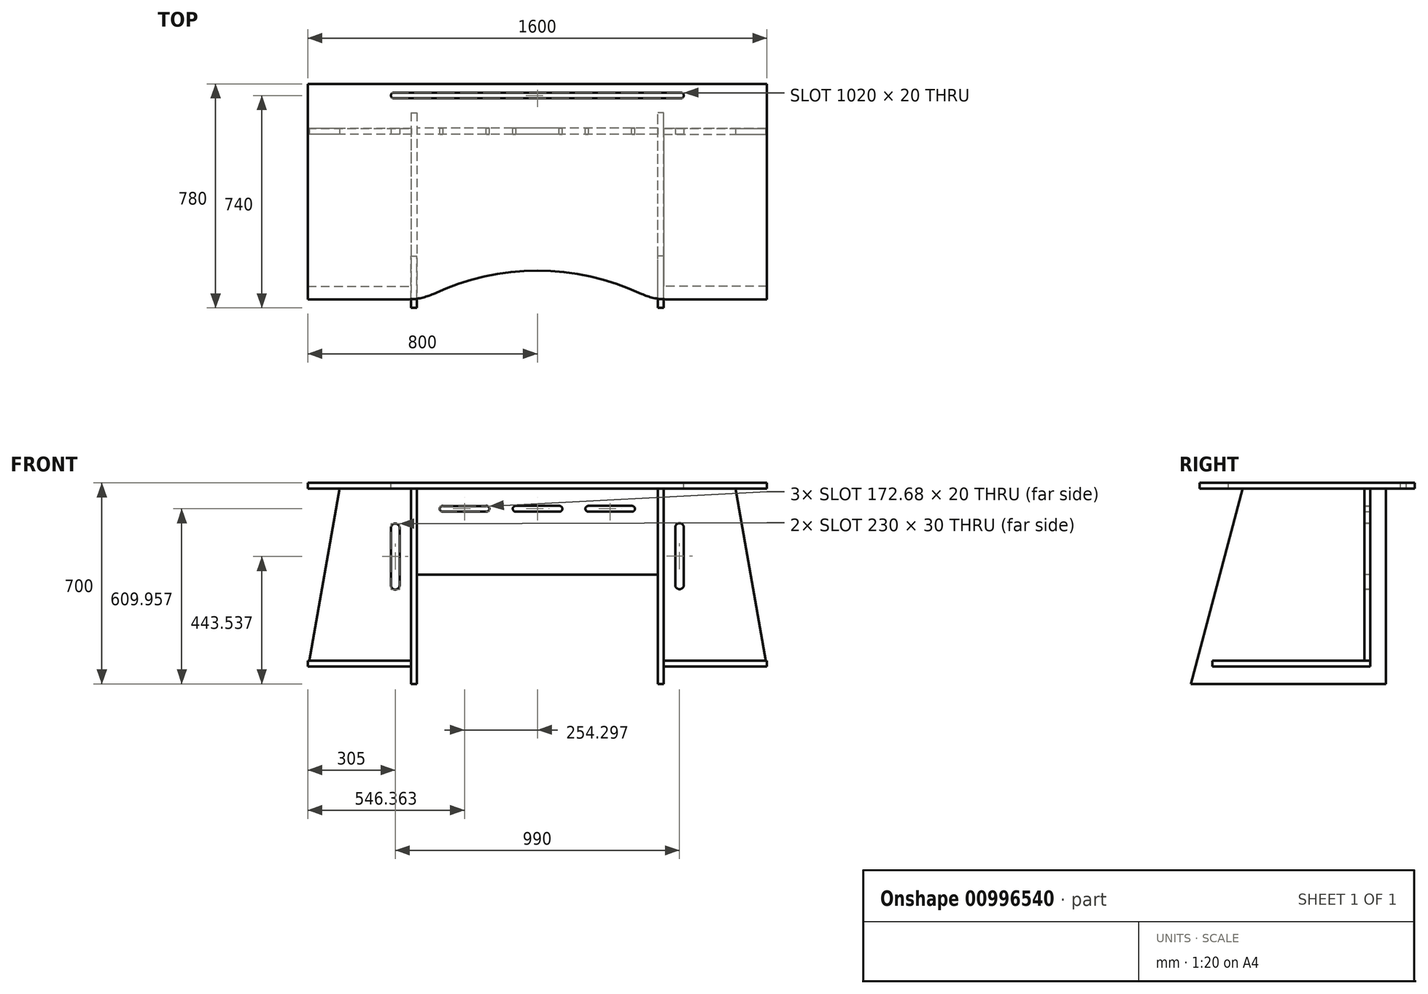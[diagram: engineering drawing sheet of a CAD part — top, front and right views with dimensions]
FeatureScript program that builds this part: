
annotation { "Feature Type Name" : "Feature", "Feature Type Description" : "" }
export const myFeature = defineFeature(function(context is Context, id is Id, definition is map)
    precondition{}
    {
        {
            var Q0;
            Q0=qCreatedBy(makeId("Top.planeOp"),FACE);
            var sketch = newSketch(context, id + "F0", { "sketchPlane" : qUnion([Q0])});
            skLineSegment(sketch, "E0.bottom", {"start": v(800, -375) * mm, "end": v(447.21, -375) * mm});
            skLineSegment(sketch, "E0.top", {"start": v(800, 375) * mm, "end": v(-800, 375) * mm});
            skLineSegment(sketch, "E0.left", {"start": v(800, -375) * mm, "end": v(800, 375) * mm});
            skLineSegment(sketch, "E0.right", {"start": v(-800, -375) * mm, "end": v(-800, 375) * mm});
            skPoint(sketch, "E0.middle", {"position": v(0, 0) * mm});
            skLineSegment(sketch, "E1", {"start": v(0, 375) * mm, "end": v(0, -375) * mm, "construction": true});
            skArc(sketch, "E2", {"start": v(362.03, -355.95) * mm, "mid": v(0, -275) * mm, "end": v(-362.03, -355.95) * mm});
            skPoint(sketch, "E3.newPointA", {"position": v(400, -375) * mm});
            skPoint(sketch, "E3.newPointB", {"position": v(-800, -375) * mm});
            skArc(sketch, "E3.filletArc", {"start": v(362.03, -355.95) * mm, "mid": v(403.57, -370.18) * mm, "end": v(447.21, -375) * mm});
            skLineSegment(sketch, "E4", {"start": v(-800, -375) * mm, "end": v(-447.21, -375) * mm});
            skPoint(sketch, "E5.visualSharp", {"position": v(-400, -375) * mm});
            skArc(sketch, "E5.filletArc", {"start": v(-447.21, -375) * mm, "mid": v(-403.57, -370.18) * mm, "end": v(-362.03, -355.95) * mm});
            skSolve(sketch);
        }
        {
            var Q0;
            Q0=makeQuery(id+"F0.imprint","IMPRINT",FACE,{"disambiguationData":[TD([[makeQuery(id+"F0.imprint","IMPRINT",EDGE,{"derivedFrom":sQuery(id+"F0.wireOp",EDGE,"E0.bottom")}),-1.0]])]});
            extrude(context, id + "F1", {"entities" : qUnion([Q0]), "depth" : 20 * mm, "offsetDistance" : 25 * mm});
        }
        {
            var Q0;
            Q0=qCreatedBy(makeId("Right.planeOp"),FACE);
            var sketch = newSketch(context, id + "F2", { "sketchPlane" : qUnion([Q0])});
            skLineSegment(sketch, "E6.bottom", {"start": v(275, 0) * mm, "end": v(-225, 0) * mm});
            skLineSegment(sketch, "E6.top", {"start": v(275, -680) * mm, "end": v(-405, -680) * mm});
            skLineSegment(sketch, "E6.left", {"start": v(275, 0) * mm, "end": v(275, -680) * mm});
            skLineSegment(sketch, "E7", {"start": v(-405, -680) * mm, "end": v(-225, 0) * mm});
            skSolve(sketch);
        }
        {
            var Q0;
            Q0=makeQuery(id+"F2.imprint","IMPRINT",FACE,{"disambiguationData":[TD([[makeQuery(id+"F2.imprint","IMPRINT",EDGE,{"derivedFrom":sQuery(id+"F2.wireOp",EDGE,"E6.bottom")}),1.0]])]});
            extrude(context, id + "F3", {"entities" : qUnion([Q0]), "oppositeDirection" : true, "depth" : 440 * mm, "offsetDistance" : 25 * mm, "hasSecondDirection" : true, "secondDirectionOppositeDirection" : true, "secondDirectionDepth" : 420 * mm});
        }
        {
            var Q0;
            Q0=qCreatedBy(makeId("Right.planeOp"),FACE);
            var sketch = newSketch(context, id + "F4", { "sketchPlane" : qUnion([Q0])});
            skLineSegment(sketch, "E8.bottom", {"start": v(-225, 0) * mm, "end": v(275, 0) * mm});
            skLineSegment(sketch, "E8.top", {"start": v(-405, -680) * mm, "end": v(275, -680) * mm});
            skLineSegment(sketch, "E8.right", {"start": v(275, 0) * mm, "end": v(275, -680) * mm});
            skLineSegment(sketch, "E9", {"start": v(-405, -680) * mm, "end": v(-225, 0) * mm});
            skPoint(sketch, "E10.orphan", {"position": v(-405, 0) * mm});
            skSolve(sketch);
        }
        {
            var Q0;
            Q0=makeQuery(id+"F4.imprint","IMPRINT",FACE,{"disambiguationData":[TD([[makeQuery(id+"F4.imprint","IMPRINT",EDGE,{"derivedFrom":sQuery(id+"F4.wireOp",EDGE,"E8.bottom")}),-1.0]])]});
            extrude(context, id + "F5", {"entities" : qUnion([Q0]), "operationType" : NewBodyOperationType.ADD, "depth" : 440 * mm, "offsetDistance" : 25 * mm, "hasSecondDirection" : true, "secondDirectionOppositeDirection" : false, "secondDirectionDepth" : 420 * mm});
        }
        {
            var Q0;
            Q0=qCreatedBy(makeId("Front.planeOp"),FACE);
            var sketch = newSketch(context, id + "F6", { "sketchPlane" : qUnion([Q0])});
            skLineSegment(sketch, "E11.bottom", {"start": v(420, 0) * mm, "end": v(-420, 0) * mm});
            skLineSegment(sketch, "E11.top", {"start": v(420, -300) * mm, "end": v(-420, -300) * mm});
            skLineSegment(sketch, "E11.left", {"start": v(420, 0) * mm, "end": v(420, -300) * mm});
            skLineSegment(sketch, "E11.right", {"start": v(-420, 0) * mm, "end": v(-420, -300) * mm});
            skSolve(sketch);
        }
        {
            var Q0;
            Q0=makeQuery(id+"F6.imprint","IMPRINT",FACE,{"disambiguationData":[TD([[makeQuery(id+"F6.imprint","IMPRINT",EDGE,{"derivedFrom":sQuery(id+"F6.wireOp",EDGE,"E11.bottom")}),1.0]])]});
            extrude(context, id + "F7", {"entities" : qUnion([Q0]), "oppositeDirection" : true, "depth" : 221 * mm, "offsetDistance" : 25 * mm, "hasSecondDirection" : true, "secondDirectionOppositeDirection" : true, "secondDirectionDepth" : 200 * mm});
        }
        {
            var Q0;
            Q0=qCreatedBy(makeId("Front.planeOp"),FACE);
            var sketch = newSketch(context, id + "F8", { "sketchPlane" : qUnion([Q0])});
            skLineSegment(sketch, "E12.bottom", {"start": v(-438.73, 0) * mm, "end": v(-688.73, 0) * mm});
            skLineSegment(sketch, "E12.top", {"start": v(-438.73, -599.48) * mm, "end": v(-794.6, -599.48) * mm});
            skLineSegment(sketch, "E12.left", {"start": v(-438.73, 0) * mm, "end": v(-438.73, -599.48) * mm});
            skLineSegment(sketch, "E13", {"start": v(-794.6, -599.48) * mm, "end": v(-794.6, -740.66) * mm, "construction": true});
            skLineSegment(sketch, "E14", {"start": v(-688.73, 0) * mm, "end": v(-794.6, -599.48) * mm});
            skPoint(sketch, "E12.right.start.orphan", {"position": v(-794.6, 0) * mm});
            skSolve(sketch);
        }
        {
            var Q0;
            Q0=makeQuery(id+"F8.imprint","IMPRINT",FACE,{"disambiguationData":[TD([[makeQuery(id+"F8.imprint","IMPRINT",EDGE,{"derivedFrom":sQuery(id+"F8.wireOp",EDGE,"E12.bottom")}),1.0]])]});
            extrude(context, id + "F9", {"entities" : qUnion([Q0]), "oppositeDirection" : true, "depth" : 220 * mm, "offsetDistance" : 25 * mm, "hasSecondDirection" : true, "secondDirectionOppositeDirection" : true, "secondDirectionDepth" : 200 * mm});
        }
        {
            var Q0;
            Q0=qCreatedBy(makeId("Right.planeOp"),FACE);
            var sketch = newSketch(context, id + "F10", { "sketchPlane" : qUnion([Q0])});
            skLineSegment(sketch, "E15.bottom", {"start": v(220.27, -599.5) * mm, "end": v(-329.73, -599.5) * mm});
            skLineSegment(sketch, "E15.top", {"start": v(220.27, -619.5) * mm, "end": v(-329.73, -619.5) * mm});
            skLineSegment(sketch, "E15.left", {"start": v(220.27, -599.5) * mm, "end": v(220.27, -619.5) * mm});
            skLineSegment(sketch, "E15.right", {"start": v(-329.73, -599.5) * mm, "end": v(-329.73, -619.5) * mm});
            skSolve(sketch);
        }
        {
            var Q0;
            Q0=makeQuery(id+"F10.imprint","IMPRINT",FACE,{"disambiguationData":[TD([[makeQuery(id+"F10.imprint","IMPRINT",EDGE,{"derivedFrom":sQuery(id+"F10.wireOp",EDGE,"E15.bottom")}),1.0]])]});
            extrude(context, id + "F11", {"entities" : qUnion([Q0]), "operationType" : NewBodyOperationType.ADD, "oppositeDirection" : true, "depth" : 800 * mm, "offsetDistance" : 25 * mm, "hasSecondDirection" : true, "secondDirectionOppositeDirection" : true, "secondDirectionDepth" : 440 * mm});
        }
        {
            var Q0;
            Q0=makeQuery(id+"F9.opExtrude","CAP_FACE",FACE,{"disambiguationData":[OSD([sQuery(id+"F8.wireOp",EDGE,"E12.bottom"),sQuery(id+"F8.wireOp",EDGE,"E12.top"),sQuery(id+"F8.wireOp",EDGE,"E12.left"),sQuery(id+"F8.wireOp",EDGE,"E14")])],"isStart":true});
            var sketch = newSketch(context, id + "F12", { "sketchPlane" : qUnion([Q0])});
            skLineSegment(sketch, "E16", {"start": v(-497.35, -207.21) * mm, "end": v(-497.35, -384.66) * mm, "construction": true});
            skLineSegment(sketch, "E17", {"start": v(-510, -136.46) * mm, "end": v(-510, -336.46) * mm});
            skLineSegment(sketch, "E18", {"start": v(-480, -136.46) * mm, "end": v(-480, -336.46) * mm});
            skArc(sketch, "E19", {"start": v(-480, -136.46) * mm, "mid": v(-495, -121.46) * mm, "end": v(-510, -136.46) * mm});
            skArc(sketch, "E20", {"start": v(-510, -336.46) * mm, "mid": v(-495, -351.46) * mm, "end": v(-480, -336.46) * mm});
            skSolve(sketch);
        }
        {
            var Q0;
            Q0=makeQuery(id+"F12.imprint","IMPRINT",FACE,{"disambiguationData":[TD([[makeQuery(id+"F12.imprint","IMPRINT",EDGE,{"derivedFrom":sQuery(id+"F12.wireOp",EDGE,"E17")}),1.0]])]});
            extrude(context, id + "F13", {"entities" : qUnion([Q0]), "operationType" : NewBodyOperationType.REMOVE, "oppositeDirection" : true, "depth" : 61 * mm, "offsetDistance" : 25 * mm});
        }
        {
            var Q0;
            Q0=makeQuery(id+"F1.opExtrude","CAP_FACE",FACE,{"disambiguationData":[OSD([sQuery(id+"F0.wireOp",EDGE,"E0.bottom"),sQuery(id+"F0.wireOp",EDGE,"E0.top"),sQuery(id+"F0.wireOp",EDGE,"E0.left"),sQuery(id+"F0.wireOp",EDGE,"E0.right"),sQuery(id+"F0.wireOp",EDGE,"E2"),sQuery(id+"F0.wireOp",EDGE,"E3.filletArc"),sQuery(id+"F0.wireOp",EDGE,"E4"),sQuery(id+"F0.wireOp",EDGE,"E5.filletArc")])],"isStart":false});
            var sketch = newSketch(context, id + "F14", { "sketchPlane" : qUnion([Q0])});
            skLineSegment(sketch, "E21", {"start": v(0, 375) * mm, "end": v(0, -425.98) * mm, "construction": true});
            skLineSegment(sketch, "E22.bottom", {"start": v(-500, 345) * mm, "end": v(500, 345) * mm});
            skLineSegment(sketch, "E22.top", {"start": v(-500, 325) * mm, "end": v(500, 325) * mm});
            skArc(sketch, "E23", {"start": v(-500, 345) * mm, "mid": v(-510, 335) * mm, "end": v(-500, 325) * mm});
            skArc(sketch, "E24", {"start": v(500, 325) * mm, "mid": v(510, 335) * mm, "end": v(500, 345) * mm});
            skSolve(sketch);
        }
        {
            var Q0;
            Q0=makeQuery(id+"F14.imprint","IMPRINT",FACE,{"disambiguationData":[TD([[makeQuery(id+"F14.imprint","IMPRINT",EDGE,{"derivedFrom":sQuery(id+"F14.wireOp",EDGE,"E22.bottom")}),-1.0]])]});
            extrude(context, id + "F15", {"entities" : qUnion([Q0]), "operationType" : NewBodyOperationType.REMOVE, "flatOperationType" : FlatOperationType.REMOVE, "endBound" : BoundingType.UP_TO_NEXT, "oppositeDirection" : true, "depth" : 64 * mm, "offsetDistance" : 25 * mm, "domain" : OperationDomain.MODEL});
        }
        {
            var Q0;
            Q0=makeQuery(id+"F9.opExtrude","CAP_FACE",FACE,{"disambiguationData":[OSD([sQuery(id+"F8.wireOp",EDGE,"E12.bottom"),sQuery(id+"F8.wireOp",EDGE,"E12.top"),sQuery(id+"F8.wireOp",EDGE,"E12.left"),sQuery(id+"F8.wireOp",EDGE,"E14")])],"isStart":true});
            var sketch = newSketch(context, id + "F16", { "sketchPlane" : qUnion([Q0])});
            skLineSegment(sketch, "E25.bottom", {"start": v(440, 0) * mm, "end": v(690, 0) * mm});
            skLineSegment(sketch, "E25.top", {"start": v(440, -599.48) * mm, "end": v(795.88, -599.48) * mm});
            skLineSegment(sketch, "E25.left", {"start": v(440, 0) * mm, "end": v(440, -599.48) * mm});
            skLineSegment(sketch, "E26", {"start": v(795.88, 14.47) * mm, "end": v(795.88, 0) * mm, "construction": true});
            skLineSegment(sketch, "E27", {"start": v(690, 0) * mm, "end": v(795.88, -599.48) * mm});
            skLineSegment(sketch, "E28.trimOffspring", {"start": v(795.88, -599.48) * mm, "end": v(795.88, -713.84) * mm, "construction": true});
            skSolve(sketch);
        }
        {
            var Q0;
            Q0=makeQuery(id+"F16.imprint","IMPRINT",FACE,{"disambiguationData":[TD([[makeQuery(id+"F16.imprint","IMPRINT",EDGE,{"derivedFrom":sQuery(id+"F16.wireOp",EDGE,"E25.bottom")}),-1.0]])]});
            extrude(context, id + "F17", {"entities" : qUnion([Q0]), "operationType" : NewBodyOperationType.ADD, "oppositeDirection" : true, "depth" : 20 * mm, "offsetDistance" : 25 * mm});
        }
        {
            var Q0;
            Q0=qCreatedBy(makeId("Right.planeOp"),FACE);
            var sketch = newSketch(context, id + "F18", { "sketchPlane" : qUnion([Q0])});
            skLineSegment(sketch, "E29.bottom", {"start": v(219.62, -599.48) * mm, "end": v(-330.38, -599.48) * mm});
            skLineSegment(sketch, "E29.top", {"start": v(219.62, -619.48) * mm, "end": v(-330.38, -619.48) * mm});
            skLineSegment(sketch, "E29.left", {"start": v(219.62, -599.48) * mm, "end": v(219.62, -619.48) * mm});
            skLineSegment(sketch, "E29.right", {"start": v(-330.38, -599.48) * mm, "end": v(-330.38, -619.48) * mm});
            skSolve(sketch);
        }
        {
            var Q0;
            Q0 = qSketchRegion(id + "F18", true);
            extrude(context, id + "F19", {"entities" : qUnion([Q0]), "operationType" : NewBodyOperationType.ADD, "depth" : 800 * mm, "offsetDistance" : 25 * mm, "hasSecondDirection" : true, "secondDirectionOppositeDirection" : false, "secondDirectionDepth" : 440 * mm});
        }
        {
            var Q0;
            Q0=makeQuery(id+"F17.opExtrude","CAP_FACE",FACE,{"disambiguationData":[OSD([sQuery(id+"F16.wireOp",EDGE,"E25.bottom"),sQuery(id+"F16.wireOp",EDGE,"E25.top"),sQuery(id+"F16.wireOp",EDGE,"E25.left"),sQuery(id+"F16.wireOp",EDGE,"E27")])],"isStart":true});
            var sketch = newSketch(context, id + "F20", { "sketchPlane" : qUnion([Q0])});
            skLineSegment(sketch, "E30.left", {"start": v(480, -135.02) * mm, "end": v(480, -335.02) * mm});
            skLineSegment(sketch, "E30.right", {"start": v(510, -135.02) * mm, "end": v(510, -335.02) * mm});
            skArc(sketch, "E31", {"start": v(510, -135.02) * mm, "mid": v(495, -120.02) * mm, "end": v(480, -135.02) * mm});
            skArc(sketch, "E32", {"start": v(480, -335.02) * mm, "mid": v(495, -350.02) * mm, "end": v(510, -335.02) * mm});
            skLineSegment(sketch, "E33", {"start": v(-496.31, -119.88) * mm, "end": v(594.19, -119.88) * mm, "construction": true});
            skSolve(sketch);
        }
        {
            var Q0;
            Q0=makeQuery(id+"F20.imprint","IMPRINT",FACE,{"disambiguationData":[TD([[makeQuery(id+"F20.imprint","IMPRINT",EDGE,{"derivedFrom":sQuery(id+"F20.wireOp",EDGE,"E30.left")}),1.0]])]});
            extrude(context, id + "F21", {"entities" : qUnion([Q0]), "operationType" : NewBodyOperationType.REMOVE, "endBound" : BoundingType.UP_TO_NEXT, "oppositeDirection" : true, "depth" : 47 * mm, "offsetDistance" : 25 * mm});
        }
        {
            var Q0;
            Q0=makeQuery(id+"F7.opExtrude","CAP_FACE",FACE,{"disambiguationData":[OSD([sQuery(id+"F6.wireOp",EDGE,"E11.bottom"),sQuery(id+"F6.wireOp",EDGE,"E11.top"),sQuery(id+"F6.wireOp",EDGE,"E11.left"),sQuery(id+"F6.wireOp",EDGE,"E11.right")])],"isStart":false});
            var sketch = newSketch(context, id + "F22", { "sketchPlane" : qUnion([Q0])});
            skLineSegment(sketch, "E34.bottom", {"start": v(-328.64, -60) * mm, "end": v(-178.64, -60) * mm});
            skLineSegment(sketch, "E34.top", {"start": v(-329.96, -80) * mm, "end": v(-177.32, -80) * mm});
            skArc(sketch, "E35", {"start": v(-328.64, -60) * mm, "mid": v(-339.98, -69.3) * mm, "end": v(-329.96, -80) * mm});
            skArc(sketch, "E36", {"start": v(-177.32, -80) * mm, "mid": v(-167.3, -69.3) * mm, "end": v(-178.64, -60) * mm});
            skLineSegment(sketch, "E37.bottom", {"start": v(178.64, -60.04) * mm, "end": v(328.64, -60.04) * mm});
            skLineSegment(sketch, "E37.top", {"start": v(177.32, -80.04) * mm, "end": v(329.96, -80.04) * mm});
            skArc(sketch, "E38", {"start": v(178.64, -60.04) * mm, "mid": v(167.3, -69.34) * mm, "end": v(177.32, -80.04) * mm});
            skArc(sketch, "E39", {"start": v(329.96, -80.04) * mm, "mid": v(339.98, -69.34) * mm, "end": v(328.64, -60.04) * mm});
            skLineSegment(sketch, "E40.bottom", {"start": v(-75.66, -60) * mm, "end": v(74.34, -60) * mm});
            skLineSegment(sketch, "E40.top", {"start": v(-76.98, -80) * mm, "end": v(75.66, -80) * mm});
            skArc(sketch, "E41", {"start": v(-75.66, -60) * mm, "mid": v(-87, -69.3) * mm, "end": v(-76.98, -80) * mm});
            skArc(sketch, "E42", {"start": v(75.66, -80) * mm, "mid": v(85.68, -69.3) * mm, "end": v(74.34, -60) * mm});
            skLineSegment(sketch, "E43", {"start": v(0, 0) * mm, "end": v(0, -233.21) * mm, "construction": true});
            skLineSegment(sketch, "E44", {"start": v(74.34, -60) * mm, "end": v(-76.98, -80) * mm, "construction": true});
            skLineSegment(sketch, "E45", {"start": v(-75.66, -60) * mm, "end": v(75.66, -80) * mm});
            skPoint(sketch, "E46", {"position": v(0, -70) * mm});
            skLineSegment(sketch, "E47", {"start": v(420, -70) * mm, "end": v(-420, -70) * mm, "construction": true});
            skSolve(sketch);
        }
        {
            var Q0;
            Q0=makeQuery(id+"F22.imprint","IMPRINT",FACE,{"disambiguationData":[TD([[makeQuery(id+"F22.imprint","IMPRINT",EDGE,{"derivedFrom":sQuery(id+"F22.wireOp",EDGE,"E34.bottom")}),-1.0]])]});
            extrude(context, id + "F23", {"entities" : qUnion([Q0]), "operationType" : NewBodyOperationType.REMOVE, "endBound" : BoundingType.UP_TO_NEXT, "oppositeDirection" : true, "depth" : 25 * mm, "offsetDistance" : 25 * mm});
        }
        {
            var Q0;
            Q0=makeQuery(id+"F22.imprint","IMPRINT",FACE,{"disambiguationData":[TD([[makeQuery(id+"F22.imprint","IMPRINT",EDGE,{"derivedFrom":sQuery(id+"F22.wireOp",EDGE,"E40.top")}),1.0]])]});
            var Q1;
            Q1=makeQuery(id+"F22.imprint","IMPRINT",FACE,{"disambiguationData":[TD([[makeQuery(id+"F22.imprint","IMPRINT",EDGE,{"derivedFrom":sQuery(id+"F22.wireOp",EDGE,"E40.bottom")}),-1.0]])]});
            var Q2;
            Q2=makeQuery(id+"F22.imprint","IMPRINT",FACE,{"disambiguationData":[TD([[makeQuery(id+"F22.imprint","IMPRINT",EDGE,{"derivedFrom":sQuery(id+"F22.wireOp",EDGE,"E37.bottom")}),-1.0]])]});
            extrude(context, id + "F24", {"entities" : qUnion([Q0, Q1, Q2]), "operationType" : NewBodyOperationType.REMOVE, "endBound" : BoundingType.UP_TO_NEXT, "oppositeDirection" : true, "depth" : 25 * mm, "offsetDistance" : 25 * mm});
        }
    });
